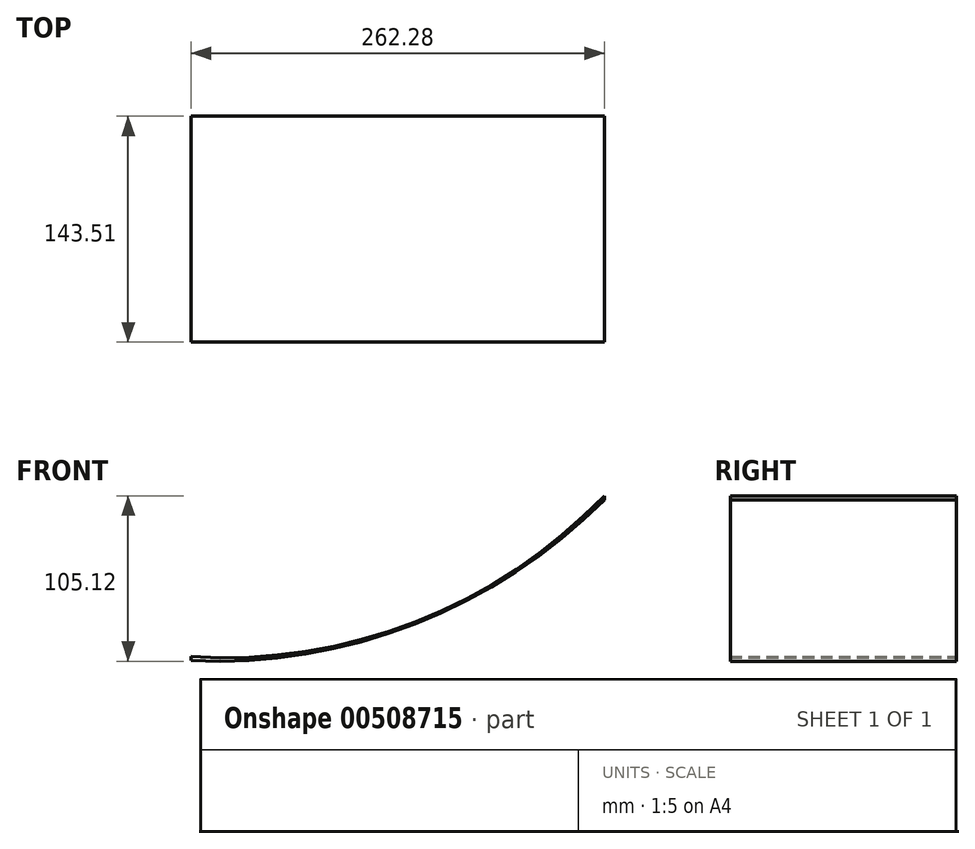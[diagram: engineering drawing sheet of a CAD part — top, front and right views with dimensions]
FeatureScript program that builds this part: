
annotation { "Feature Type Name" : "Feature", "Feature Type Description" : "" }
export const myFeature = defineFeature(function(context is Context, id is Id, definition is map)
    precondition{}
    {
        {
            var Q0;
            Q0=qCreatedBy(makeId("Front.planeOp"),FACE);
            var sketch = newSketch(context, id + "F0", { "sketchPlane" : qUnion([Q0])});
            skArc(sketch, "E0", {"start": v(-111.78, 3.9) * mm, "mid": v(30.2, 27.2) * mm, "end": v(150.5, 106.1) * mm});
            skArc(sketch, "E1", {"start": v(-111.78, 6.44) * mm, "mid": v(30.69, 28.48) * mm, "end": v(150.5, 108.65) * mm});
            skLineSegment(sketch, "E2", {"start": v(-111.78, 6.44) * mm, "end": v(-111.78, 3.9) * mm});
            skLineSegment(sketch, "E3", {"start": v(150.5, 108.65) * mm, "end": v(150.5, 106.1) * mm});
            skSolve(sketch);
        }
        {
            var Q0;
            Q0=makeQuery(id+"F0.imprint","IMPRINT",FACE,{"disambiguationData":[TD([[makeQuery(id+"F0.imprint","IMPRINT",EDGE,{"derivedFrom":sQuery(id+"F0.wireOp",EDGE,"E0")}),1.0]])]});
            extrude(context, id + "F1", {"entities" : qUnion([Q0]), "depth" : 143.5 * mm});
        }
    });
